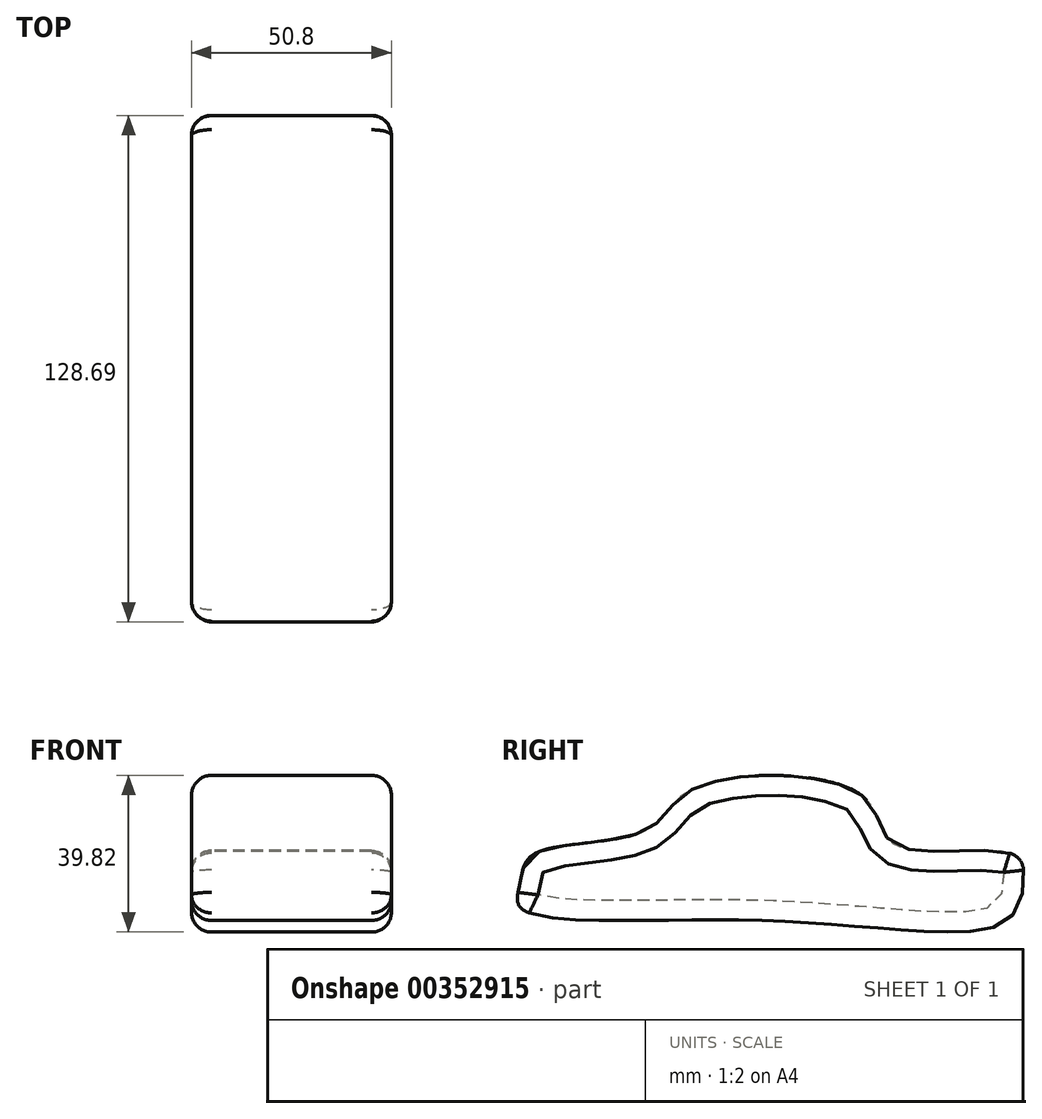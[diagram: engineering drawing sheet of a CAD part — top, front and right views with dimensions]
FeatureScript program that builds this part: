
annotation { "Feature Type Name" : "Feature", "Feature Type Description" : "" }
export const myFeature = defineFeature(function(context is Context, id is Id, definition is map)
    precondition{}
    {
        {
            var Q0;
            Q0=qCreatedBy(makeId("Right.planeOp"),FACE);
            var sketch = newSketch(context, id + "F0", { "sketchPlane" : qUnion([Q0])});
            skFitSpline(sketch, "E0", {"points": [v(-60.84, 7.23) * mm, v(-64.28, 0) * mm, v(-64.05, -6.54) * mm, v(0, -9.76) * mm, v(58.54, -10.22) * mm, v(63.6, 0) * mm, v(60.61, 7.23) * mm, v(31, 9.53) * mm, v(22.73, 21.93) * mm, v(-20.43, 23.76) * mm, v(-32.37, 13.2) * mm, v(-60.84, 7.23) * mm]});
            skSolve(sketch);
        }
        {
            var Q0;
            Q0=makeQuery(id+"F0.imprint","IMPRINT",FACE,{"disambiguationData":[TD([[makeQuery(id+"F0.imprint","IMPRINT",EDGE,{"derivedFrom":sQuery(id+"F0.wireOp",EDGE,"E0")}),1.0]])]});
            extrude(context, id + "F1", {"entities" : qUnion([Q0]), "endBound" : BoundingType.SYMMETRIC, "depth" : 50.8 * mm});
        }
        {
            var Q0;
            Q0=makeQuery(id+"F1.opExtrude","CAP_FACE",FACE,{"disambiguationData":[OSD([sQuery(id+"F0.wireOp",EDGE,"E0")])],"isStart":false});
            var Q1;
            Q1=makeQuery(id+"F1.opExtrude","CAP_FACE",FACE,{"disambiguationData":[OSD([sQuery(id+"F0.wireOp",EDGE,"E0")])],"isStart":true});
            fillet(context, id + "F2", {"entities" : qUnion([Q0, Q1]), "radius" : 5.08 * mm, "tangentPropagation" : true, "allowEdgeOverflow" : false});
        }
    });
